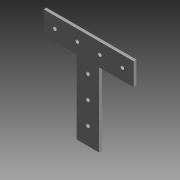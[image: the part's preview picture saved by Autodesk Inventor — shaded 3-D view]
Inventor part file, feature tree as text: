
AUTODESK INVENTOR PART (.ipt)
format: ipt  version: 2014 (Build 180170000, 170)  size: 156,160 bytes
history: native  units: in
note: dims shown in document units (in); Inventor stores cm internally (conversion verified against a paired STEP export)
features: reference x7, sheet_metal_op x4, sketch x3, other x2, hole x1
ambient origin geometry x8: Origin, YZ Plane, XZ Plane, XY Plane, X Axis, Y Axis, Z Axis, Center Point
bodies: Solid1 (feature_tree)
feature tree (17):
  sheet_metal_op  "Face1"
  sheet_metal_op  "Flange2"
  hole  "Hole2"  [1 undecoded]
  sketch  "Sketch1"  dims[d0=0.125in d19=0.125in]
  reference  "Reference1"
  reference  "Reference2"
  reference  "Reference3"
  reference  "Reference4"
  other  "Plate1"
  reference  "Reference5"
  reference  "Reference6"
  reference  "Reference7"
  sketch  "Sketch4"  dims[d20=0.0625in]
  other  "Plate3"
  sheet_metal_op  "Bend2"
  sheet_metal_op  "Corner2"
  sketch  "Sketch5"  dims[d21=0.25in d22=0.125in d23=3.5in d24=90.0deg d25=0.05in d26=0.5in d27=0.125in d28=0.125in d29=0.266in d30=0.266in d31=0.75in d32=0.375in d33=0.25in d34=0.5635in d35=0.125in d36=0.8108in]
note: 1 required parameter value undecoded (feature->parameter linkage not recoverable at this tier; creation-order binding heuristic only, values carry confidence <= 0.55)
